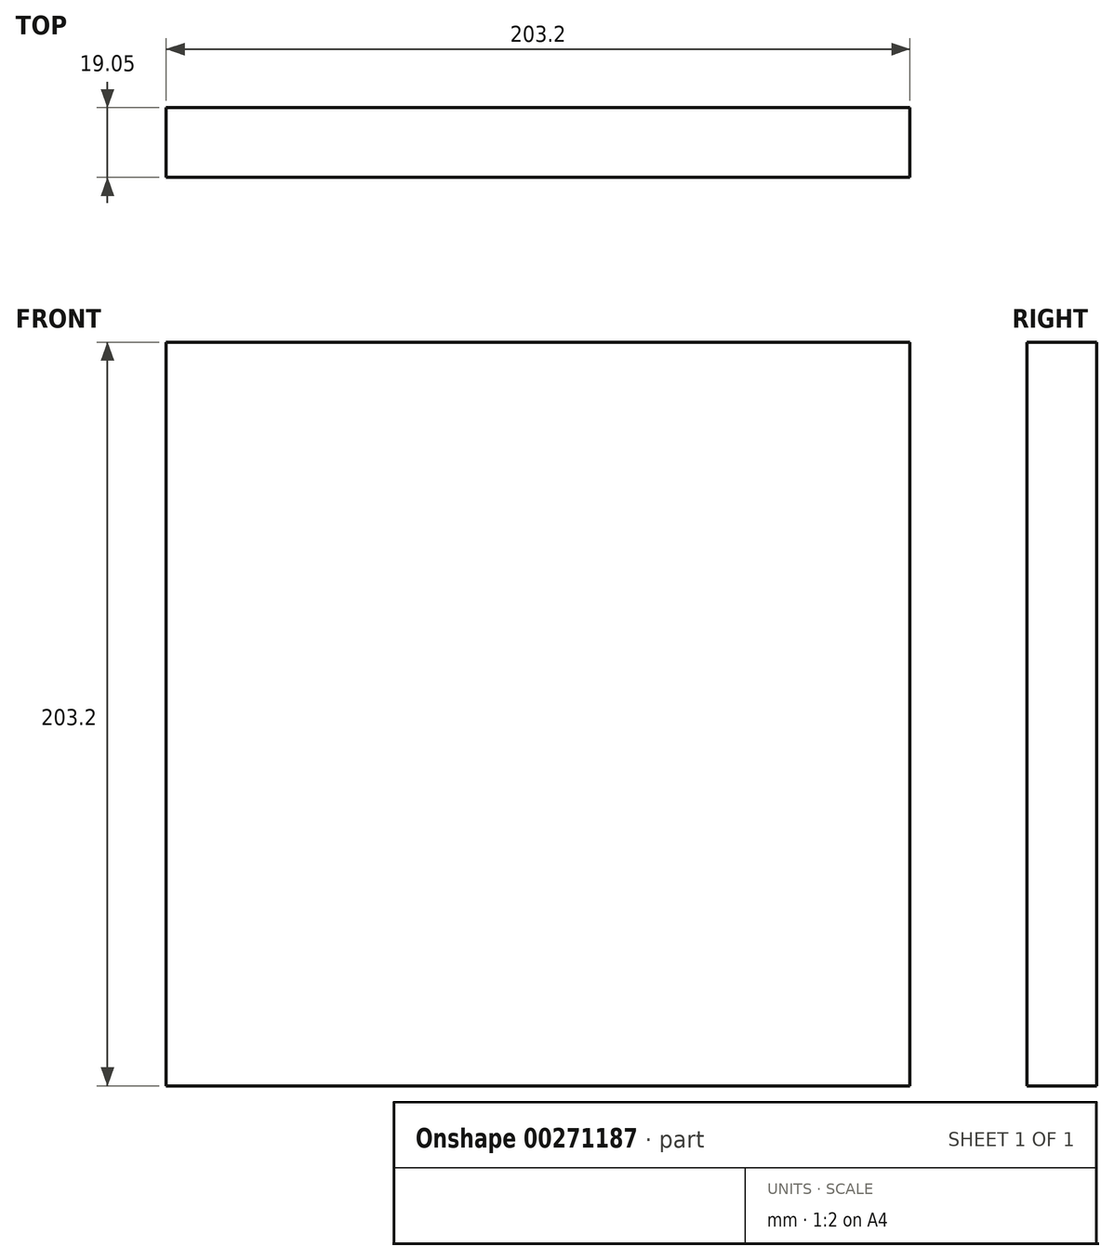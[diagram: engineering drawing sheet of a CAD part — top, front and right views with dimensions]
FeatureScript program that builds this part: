
annotation { "Feature Type Name" : "Feature", "Feature Type Description" : "" }
export const myFeature = defineFeature(function(context is Context, id is Id, definition is map)
    precondition{}
    {
        {
            var Q0;
            Q0=qCreatedBy(makeId("Front.planeOp"),FACE);
            var sketch = newSketch(context, id + "F0", { "sketchPlane" : qUnion([Q0])});
            skLineSegment(sketch, "E0.bottom", {"start": v(101.6, 101.6) * mm, "end": v(-101.6, 101.6) * mm});
            skLineSegment(sketch, "E0.top", {"start": v(101.6, -101.6) * mm, "end": v(-101.6, -101.6) * mm});
            skLineSegment(sketch, "E0.left", {"start": v(101.6, 101.6) * mm, "end": v(101.6, -101.6) * mm});
            skLineSegment(sketch, "E0.right", {"start": v(-101.6, 101.6) * mm, "end": v(-101.6, -101.6) * mm});
            skPoint(sketch, "E0.middle", {"position": v(0, 0) * mm});
            skSolve(sketch);
        }
        {
            var Q0;
            Q0=makeQuery(id+"F0.imprint","IMPRINT",FACE,{"disambiguationData":[TD([[makeQuery(id+"F0.imprint","IMPRINT",EDGE,{"derivedFrom":sQuery(id+"F0.wireOp",EDGE,"E0.bottom")}),1.0]])]});
            extrude(context, id + "F1", {"entities" : qUnion([Q0]), "depth" : 19.05 * mm});
        }
    });
